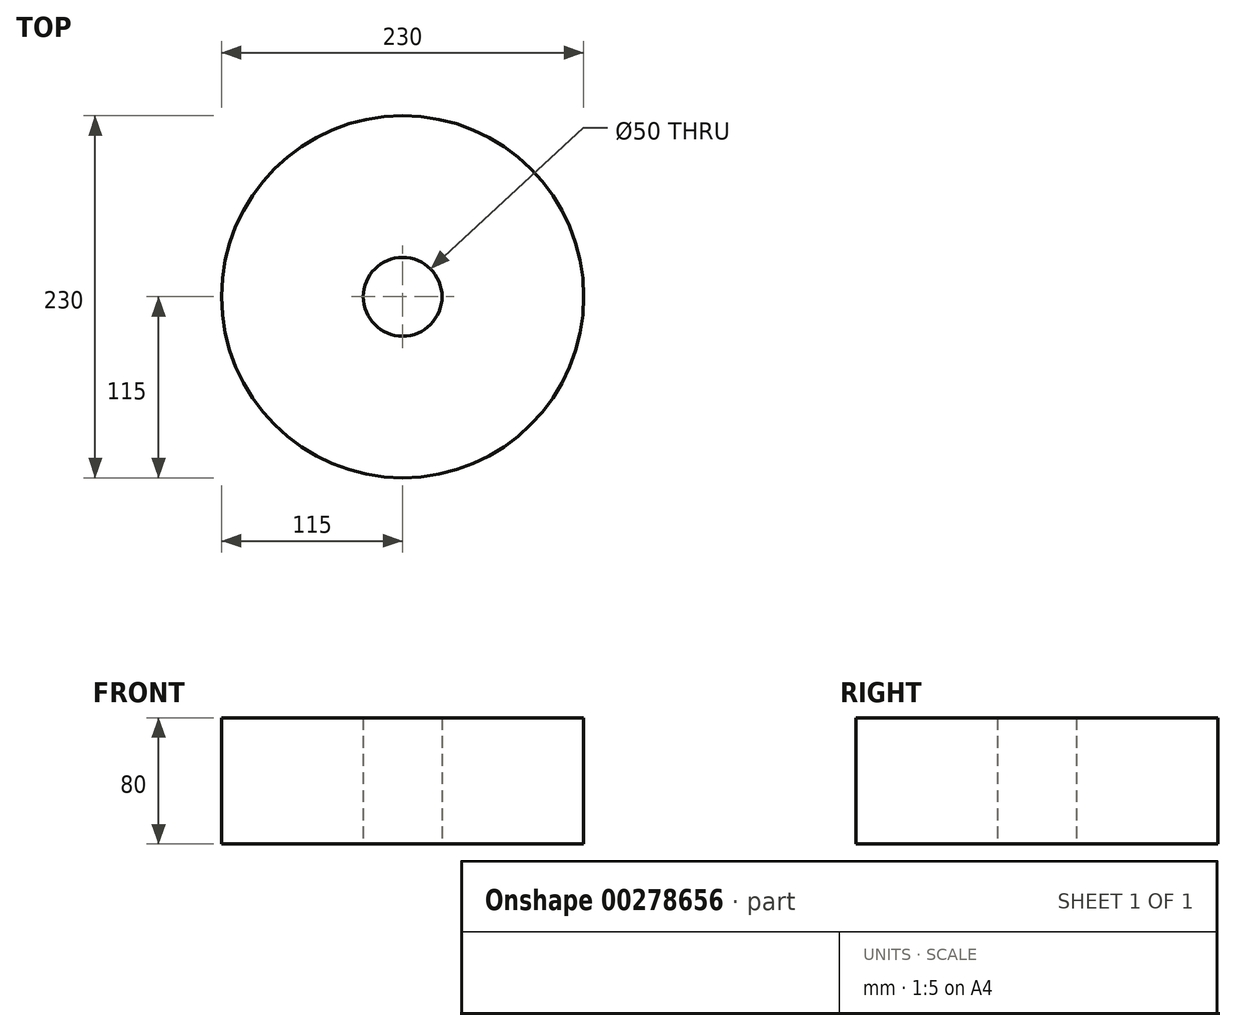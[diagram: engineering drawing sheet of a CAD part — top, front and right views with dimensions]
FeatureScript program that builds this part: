
annotation { "Feature Type Name" : "Feature", "Feature Type Description" : "" }
export const myFeature = defineFeature(function(context is Context, id is Id, definition is map)
    precondition{}
    {
        {
            var Q0;
            Q0=qCreatedBy(makeId("Top.planeOp"),FACE);
            var sketch = newSketch(context, id + "F0", { "sketchPlane" : qUnion([Q0])});
            skCircle(sketch, "E0", {"center": v(0, 0) * mm, "radius": 115 * mm});
            skCircle(sketch, "E1", {"center": v(0, 0) * mm, "radius": 25 * mm});
            skSolve(sketch);
        }
        {
            var Q0;
            Q0=makeQuery(id+"F0.imprint","IMPRINT",FACE,{"disambiguationData":[TD([[makeQuery(id+"F0.imprint","IMPRINT",EDGE,{"derivedFrom":sQuery(id+"F0.wireOp",EDGE,"E0")}),1.0]])]});
            extrude(context, id + "F1", {"entities" : qUnion([Q0]), "depth" : 80 * mm});
        }
    });
